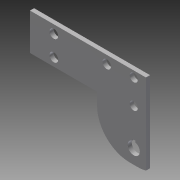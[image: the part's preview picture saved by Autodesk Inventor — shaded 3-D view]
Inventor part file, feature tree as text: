
AUTODESK INVENTOR PART (.ipt)
format: ipt  version: 2013 (Build 170138000, 138)  size: 178,688 bytes
history: native  units: in
note: dims shown in document units (in); Inventor stores cm internally (conversion verified against a paired STEP export)
features: sketch x6, other x6, reference x6, sheet_metal_op x1, extrude x1, fillet x1, plane x1
ambient origin geometry x8: Origin, YZ Plane, XZ Plane, XY Plane, X Axis, Y Axis, Z Axis, Center Point
feature tree (22):
  sheet_metal_op  "Face3"
  extrude  "Extrusion2"  Depth=0.25in
  sketch  "Sketch8"  dims[d8=0.125in]
  fillet  "Fillet1"  Radius=0.295in
  sketch  "Sketch11"  dims[d60=2.5in]
  plane  "Work Plane2"
  other  "Plate6"
  sketch  "Sketch7"  dims[d3=0.295in d4=0.25in d5=0.295in]
  reference  "Reference1"
  reference  "Reference2"
  sketch  "Sketch9"  dims[d19=0.25in]
  sketch  "Sketch10"  dims[d56=0.125in]
  reference  "Reference3"
  reference  "Reference4"
  sketch  "Sketch12"  dims[d61=0.4375in d62=0.375in d63=0.125in d67=0.125in d68=0.0in d69=2.053in d70=0.0in d71=1.125in d72=2.053in d75=0.125in d76=0.0in d77=0.125in d78=0.0in d79=0.125in d80=0.0in d81=1.0in d82=0.0469in d86=0.0938in d87=0.0469in d88=0.75in d89=0.125in d90=0.0in]
  reference  "Reference5"
  reference  "Reference6"
  other  "Cut1"
  other  "Cut3"
  other  "Cut4"
  other  "Cut5"
  other  "Cut6"
